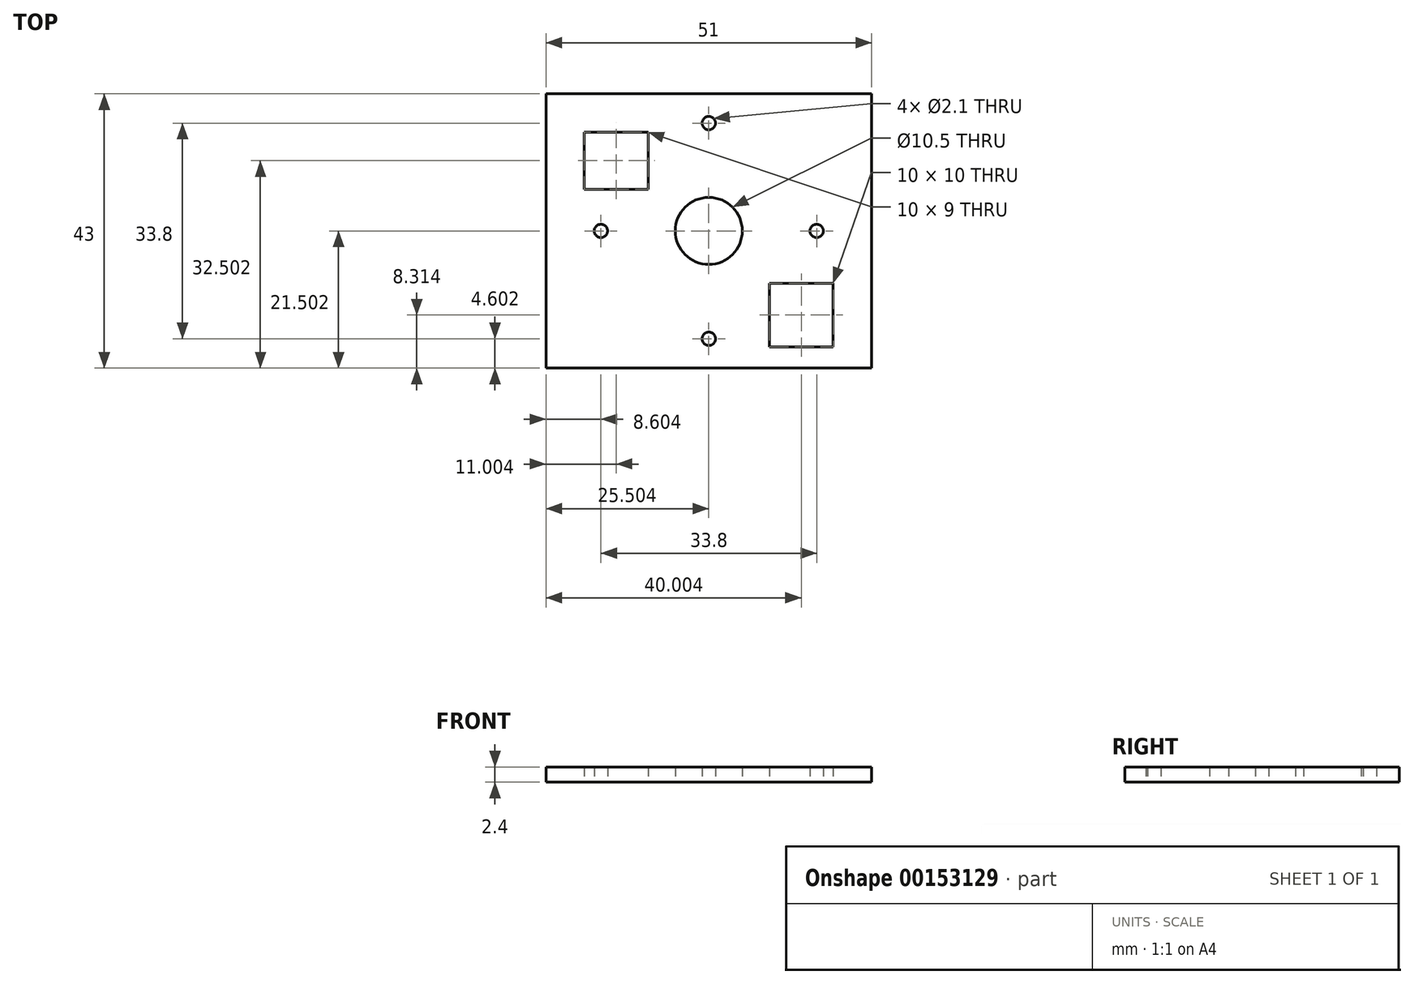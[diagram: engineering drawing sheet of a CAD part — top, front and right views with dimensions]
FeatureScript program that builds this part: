
annotation { "Feature Type Name" : "Feature", "Feature Type Description" : "" }
export const myFeature = defineFeature(function(context is Context, id is Id, definition is map)
    precondition{}
    {
        {
            var Q0;
            Q0=qCreatedBy(makeId("Top.planeOp"),FACE);
            var sketch = newSketch(context, id + "F0", { "sketchPlane" : qUnion([Q0])});
            skLineSegment(sketch, "E0.bottom", {"start": v(-62.38, 51) * mm, "end": v(-11.38, 51) * mm});
            skLineSegment(sketch, "E0.top", {"start": v(-62.38, 8) * mm, "end": v(-11.38, 8) * mm});
            skLineSegment(sketch, "E0.left", {"start": v(-62.38, 51) * mm, "end": v(-62.38, 8) * mm});
            skLineSegment(sketch, "E0.right", {"start": v(-11.38, 51) * mm, "end": v(-11.38, 8) * mm});
            skLineSegment(sketch, "E1", {"start": v(-36.88, 51) * mm, "end": v(-36.88, 8) * mm, "construction": true});
            skLineSegment(sketch, "E2", {"start": v(-11.38, 29.5) * mm, "end": v(-62.38, 29.5) * mm, "construction": true});
            skCircle(sketch, "E3", {"center": v(-36.88, 29.5) * mm, "radius": 5.25 * mm});
            skCircle(sketch, "E4", {"center": v(-36.88, 29.5) * mm, "radius": 16.9 * mm, "construction": true});
            skCircle(sketch, "E5", {"center": v(-19.98, 29.5) * mm, "radius": 1.05 * mm});
            skCircle(sketch, "E6", {"center": v(-36.88, 46.4) * mm, "radius": 1.05 * mm});
            skCircle(sketch, "E7", {"center": v(-53.78, 29.5) * mm, "radius": 1.05 * mm});
            skCircle(sketch, "E8", {"center": v(-36.88, 12.6) * mm, "radius": 1.05 * mm});
            skCircle(sketch, "E9", {"center": v(-62.38, 51) * mm, "radius": 6 * mm, "construction": true});
            skCircle(sketch, "E10", {"center": v(-11.38, 8) * mm, "radius": 6 * mm, "construction": true});
            skLineSegment(sketch, "E11", {"start": v(-62.38, 45) * mm, "end": v(-11.38, 45) * mm, "construction": true});
            skLineSegment(sketch, "E12", {"start": v(-56.38, 51) * mm, "end": v(-56.38, 8) * mm, "construction": true});
            skLineSegment(sketch, "E13", {"start": v(-11.38, 14) * mm, "end": v(-62.38, 14) * mm, "construction": true});
            skLineSegment(sketch, "E14", {"start": v(-17.38, 8) * mm, "end": v(-17.38, 51) * mm, "construction": true});
            skLineSegment(sketch, "E15.bottom", {"start": v(-56.38, 45) * mm, "end": v(-46.38, 45) * mm});
            skLineSegment(sketch, "E15.top", {"start": v(-56.38, 36) * mm, "end": v(-46.38, 36) * mm});
            skLineSegment(sketch, "E15.left", {"start": v(-56.38, 45) * mm, "end": v(-56.38, 36) * mm});
            skLineSegment(sketch, "E15.right", {"start": v(-46.38, 45) * mm, "end": v(-46.38, 36) * mm});
            skLineSegment(sketch, "E16.bottom", {"start": v(-17.38, 11.3) * mm, "end": v(-27.38, 11.3) * mm});
            skLineSegment(sketch, "E16.top", {"start": v(-17.38, 21.3) * mm, "end": v(-27.38, 21.3) * mm});
            skLineSegment(sketch, "E16.left", {"start": v(-17.38, 11.3) * mm, "end": v(-17.38, 21.3) * mm});
            skLineSegment(sketch, "E16.right", {"start": v(-27.38, 11.3) * mm, "end": v(-27.38, 21.3) * mm});
            skSolve(sketch);
        }
        {
            var Q0;
            Q0=makeQuery(id+"F0.imprint","IMPRINT",FACE,{"disambiguationData":[TD([[makeQuery(id+"F0.imprint","IMPRINT",EDGE,{"derivedFrom":sQuery(id+"F0.wireOp",EDGE,"E0.bottom")}),-1.0]])]});
            extrude(context, id + "F1", {"entities" : qUnion([Q0]), "depth" : 2.4 * mm});
        }
    });
